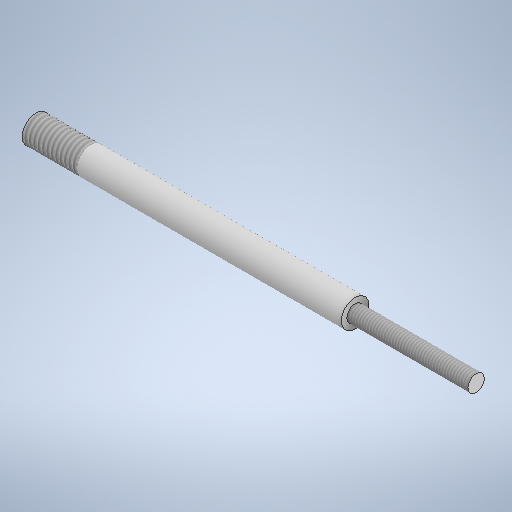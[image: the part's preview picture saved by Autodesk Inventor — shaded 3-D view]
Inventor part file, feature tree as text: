
AUTODESK INVENTOR PART (.ipt)
format: ipt  version: 2025.1 (Build 291241000, 241)  size: 279,040 bytes
history: native  units: mm
features: thread x2, revolve x1, sketch x1
ambient origin geometry x8: Origin, YZ Plane, XZ Plane, XY Plane, X Axis, Y Axis, Z Axis, Center Point
bodies: Solid1 (feature_tree)
feature tree (4):
  revolve  "Revolution1"  [1 undecoded]
  thread  "Thread1"  [1 undecoded]
  thread  "Thread2"  [1 undecoded]
  sketch  "Sketch1"  dims[d0=58.0mm d1=22.0mm d2=3.0mm d3=5.0mm d4=90.0deg d5=22.0mm d6=0.0mm d7=10.0mm d8=0.0mm]
note: 3 required parameter values undecoded (feature->parameter linkage not recoverable at this tier; creation-order binding heuristic only, values carry confidence <= 0.55)